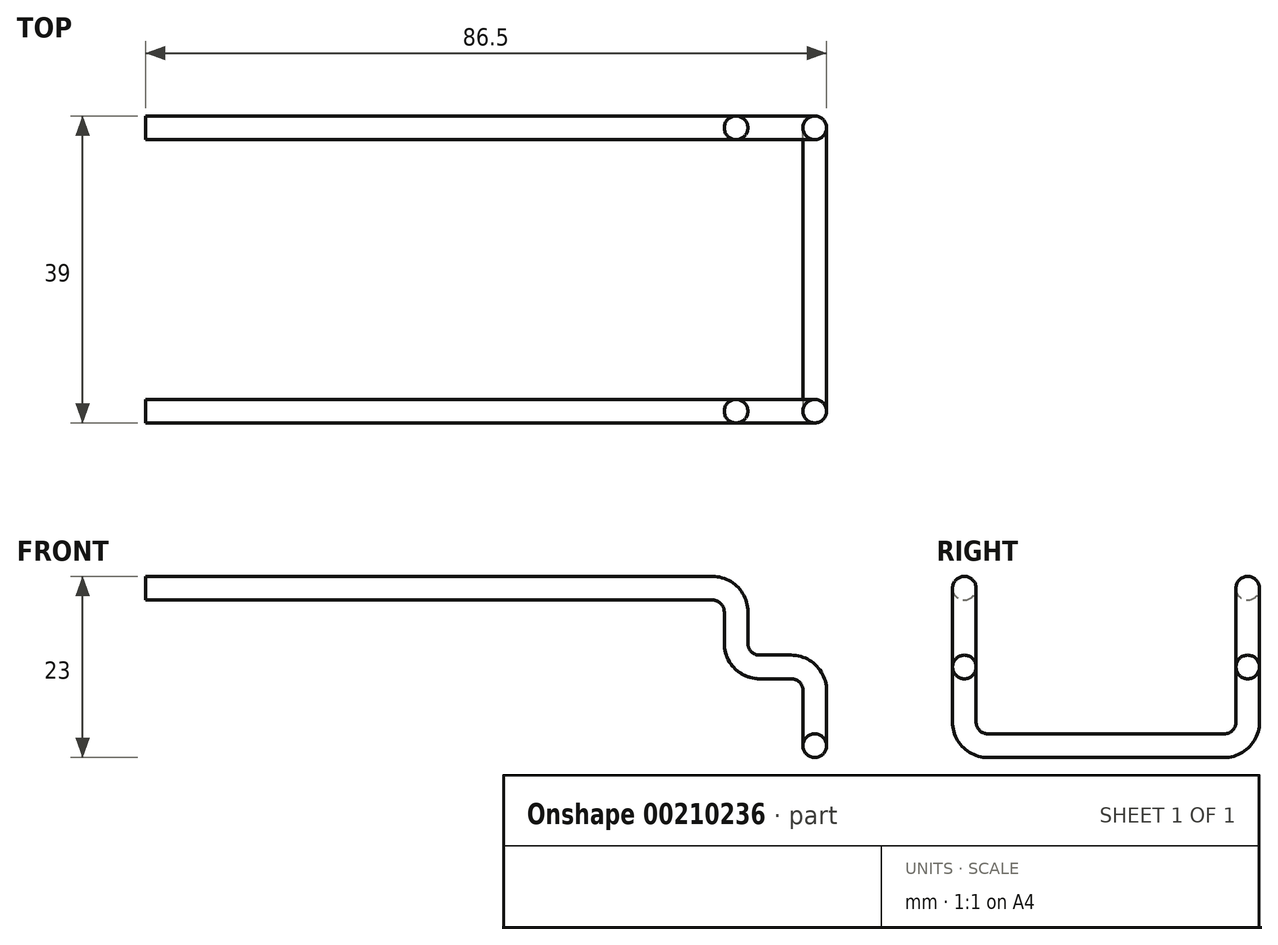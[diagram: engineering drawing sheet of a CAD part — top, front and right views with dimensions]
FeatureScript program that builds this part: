
annotation { "Feature Type Name" : "Feature", "Feature Type Description" : "" }
export const myFeature = defineFeature(function(context is Context, id is Id, definition is map)
    precondition{}
    {
        {
            var Q0;
            Q0=qCreatedBy(makeId("Front.planeOp"),FACE);
            var sketch = newSketch(context, id + "F0", { "sketchPlane" : qUnion([Q0])});
            skLineSegment(sketch, "E0", {"start": v(-46.79, 16.45) * mm, "end": v(28.21, 16.45) * mm});
            skLineSegment(sketch, "E1", {"start": v(28.21, 16.45) * mm, "end": v(28.21, 6.45) * mm});
            skLineSegment(sketch, "E2", {"start": v(28.21, 6.45) * mm, "end": v(38.21, 6.45) * mm});
            skLineSegment(sketch, "E3", {"start": v(38.21, 6.45) * mm, "end": v(38.21, -3.55) * mm});
            skLineSegment(sketch, "E4", {"start": v(38.21, -3.55) * mm, "end": v(-46.79, -3.55) * mm});
            skLineSegment(sketch, "E5", {"start": v(-46.79, -3.55) * mm, "end": v(-46.79, 16.45) * mm});
            skSolve(sketch);
        }
        {
            var Q0;
            Q0 = qSketchRegion(id + "F0", true);
            extrude(context, id + "F1", {"entities" : qUnion([Q0]), "endBound" : BoundingType.SYMMETRIC, "depth" : 36 * mm});
        }
        {
            var Q0;
            Q0=makeQuery(id+"F1.opExtrude","SWEPT_FACE",FACE,{"disambiguationData":[OSD([sQuery(id+"F0.wireOp",EDGE,"E5")])]});
            var sketch = newSketch(context, id + "F2", { "sketchPlane" : qUnion([Q0])});
            skCircle(sketch, "E6", {"center": v(18, 16.45) * mm, "radius": 1.5 * mm});
            skSolve(sketch);
        }
        {
            var Q0;
            Q0=makeQuery(id+"F1.opExtrude","SWEPT_EDGE",EDGE,{"disambiguationData":[OSD([sQuery(id+"F0.wireOp",EDGE,"E0"),sQuery(id+"F0.wireOp",EDGE,"E1")])]});
            var Q1;
            Q1=makeQuery(id+"F1.opExtrude","SWEPT_EDGE",EDGE,{"disambiguationData":[OSD([sQuery(id+"F0.wireOp",EDGE,"E1"),sQuery(id+"F0.wireOp",EDGE,"E2")])]});
            var Q2;
            Q2=makeQuery(id+"F1.opExtrude","SWEPT_EDGE",EDGE,{"disambiguationData":[OSD([sQuery(id+"F0.wireOp",EDGE,"E2"),sQuery(id+"F0.wireOp",EDGE,"E3")])]});
            var Q3;
            Q3=makeQuery(id+"F1.opExtrude","CAP_EDGE",EDGE,{"disambiguationData":[OSD([sQuery(id+"F0.wireOp",EDGE,"E4")])],"isStart":false});
            var Q4;
            Q4=makeQuery(id+"F1.opExtrude","CAP_EDGE",EDGE,{"disambiguationData":[OSD([sQuery(id+"F0.wireOp",EDGE,"E4")])],"isStart":true});
            fillet(context, id + "F3", {"entities" : qUnion([Q0, Q1, Q2, Q3, Q4]), "radius" : 3 * mm, "tangentPropagation" : true, "allowEdgeOverflow" : false});
        }
        {
            var Q0;
            Q0 = qSketchRegion(id + "F2", true);
            var Q1;
            Q1=makeQuery(id+"F1.opExtrude","CAP_EDGE",EDGE,{"disambiguationData":[OSD([sQuery(id+"F0.wireOp",EDGE,"E0")])],"isStart":false});
            var Q2;
            {var subQ0=sQuery(id+"F0.wireOp",EDGE,"E1");var subQ1=sQuery(id+"F0.wireOp",EDGE,"E0");Q2=makeQuery(id+"F3.opFillet","BLEND_EDGE",EDGE,{"blendedFrom":[makeQuery(id+"F1.opExtrude","SWEPT_EDGE",EDGE,{"disambiguationData":[OSD([subQ1,subQ0])]}),makeQuery(id+"F1.opExtrude","CAP_FACE",FACE,{"disambiguationData":[OSD([subQ1,subQ0,sQuery(id+"F0.wireOp",EDGE,"E2"),sQuery(id+"F0.wireOp",EDGE,"E3"),sQuery(id+"F0.wireOp",EDGE,"E4"),sQuery(id+"F0.wireOp",EDGE,"E5")])],"isStart":false})],"blendedInto":[makeQuery(id+"F1.opExtrude","CAP_FACE",FACE,{"disambiguationData":[OSD([subQ1,subQ0,sQuery(id+"F0.wireOp",EDGE,"E2"),sQuery(id+"F0.wireOp",EDGE,"E3"),sQuery(id+"F0.wireOp",EDGE,"E4"),sQuery(id+"F0.wireOp",EDGE,"E5")])],"isStart":false})]});}
            var Q3;
            Q3=makeQuery(id+"F1.opExtrude","CAP_EDGE",EDGE,{"disambiguationData":[OSD([sQuery(id+"F0.wireOp",EDGE,"E1")])],"isStart":false});
            var Q4;
            {var subQ0=sQuery(id+"F0.wireOp",EDGE,"E2");var subQ1=sQuery(id+"F0.wireOp",EDGE,"E1");Q4=makeQuery(id+"F3.opFillet","BLEND_EDGE",EDGE,{"blendedFrom":[makeQuery(id+"F1.opExtrude","SWEPT_EDGE",EDGE,{"disambiguationData":[OSD([subQ1,subQ0])]}),makeQuery(id+"F1.opExtrude","CAP_FACE",FACE,{"disambiguationData":[OSD([sQuery(id+"F0.wireOp",EDGE,"E0"),subQ1,subQ0,sQuery(id+"F0.wireOp",EDGE,"E3"),sQuery(id+"F0.wireOp",EDGE,"E4"),sQuery(id+"F0.wireOp",EDGE,"E5")])],"isStart":false})],"blendedInto":[makeQuery(id+"F1.opExtrude","CAP_FACE",FACE,{"disambiguationData":[OSD([sQuery(id+"F0.wireOp",EDGE,"E0"),subQ1,subQ0,sQuery(id+"F0.wireOp",EDGE,"E3"),sQuery(id+"F0.wireOp",EDGE,"E4"),sQuery(id+"F0.wireOp",EDGE,"E5")])],"isStart":false})]});}
            var Q5;
            Q5=makeQuery(id+"F1.opExtrude","CAP_EDGE",EDGE,{"disambiguationData":[OSD([sQuery(id+"F0.wireOp",EDGE,"E2")])],"isStart":false});
            var Q6;
            {var subQ0=sQuery(id+"F0.wireOp",EDGE,"E3");var subQ1=sQuery(id+"F0.wireOp",EDGE,"E2");Q6=makeQuery(id+"F3.opFillet","BLEND_EDGE",EDGE,{"blendedFrom":[makeQuery(id+"F1.opExtrude","SWEPT_EDGE",EDGE,{"disambiguationData":[OSD([subQ1,subQ0])]}),makeQuery(id+"F1.opExtrude","CAP_FACE",FACE,{"disambiguationData":[OSD([sQuery(id+"F0.wireOp",EDGE,"E0"),sQuery(id+"F0.wireOp",EDGE,"E1"),subQ1,subQ0,sQuery(id+"F0.wireOp",EDGE,"E4"),sQuery(id+"F0.wireOp",EDGE,"E5")])],"isStart":false})],"blendedInto":[makeQuery(id+"F1.opExtrude","CAP_FACE",FACE,{"disambiguationData":[OSD([sQuery(id+"F0.wireOp",EDGE,"E0"),sQuery(id+"F0.wireOp",EDGE,"E1"),subQ1,subQ0,sQuery(id+"F0.wireOp",EDGE,"E4"),sQuery(id+"F0.wireOp",EDGE,"E5")])],"isStart":false})]});}
            var Q7;
            Q7=makeQuery(id+"F1.opExtrude","CAP_EDGE",EDGE,{"disambiguationData":[OSD([sQuery(id+"F0.wireOp",EDGE,"E3")])],"isStart":false});
            var Q8;
            Q8=makeQuery(id+"F3.opFillet","BLEND_EDGE",EDGE,{"blendedFrom":[makeQuery(id+"F1.opExtrude","CAP_EDGE",EDGE,{"disambiguationData":[OSD([sQuery(id+"F0.wireOp",EDGE,"E4")])],"isStart":false}),makeQuery(id+"F1.opExtrude","SWEPT_FACE",FACE,{"disambiguationData":[OSD([sQuery(id+"F0.wireOp",EDGE,"E3")])]})],"blendedInto":[makeQuery(id+"F1.opExtrude","SWEPT_FACE",FACE,{"disambiguationData":[OSD([sQuery(id+"F0.wireOp",EDGE,"E3")])]})]});
            var Q9;
            Q9=makeQuery(id+"F1.opExtrude","SWEPT_EDGE",EDGE,{"disambiguationData":[OSD([sQuery(id+"F0.wireOp",EDGE,"E3"),sQuery(id+"F0.wireOp",EDGE,"E4")])]});
            var Q10;
            Q10=makeQuery(id+"F3.opFillet","BLEND_EDGE",EDGE,{"blendedFrom":[makeQuery(id+"F1.opExtrude","CAP_EDGE",EDGE,{"disambiguationData":[OSD([sQuery(id+"F0.wireOp",EDGE,"E4")])],"isStart":true}),makeQuery(id+"F1.opExtrude","SWEPT_FACE",FACE,{"disambiguationData":[OSD([sQuery(id+"F0.wireOp",EDGE,"E3")])]})],"blendedInto":[makeQuery(id+"F1.opExtrude","SWEPT_FACE",FACE,{"disambiguationData":[OSD([sQuery(id+"F0.wireOp",EDGE,"E3")])]})]});
            var Q11;
            Q11=makeQuery(id+"F1.opExtrude","CAP_EDGE",EDGE,{"disambiguationData":[OSD([sQuery(id+"F0.wireOp",EDGE,"E3")])],"isStart":true});
            var Q12;
            {var subQ0=sQuery(id+"F0.wireOp",EDGE,"E3");var subQ1=sQuery(id+"F0.wireOp",EDGE,"E2");Q12=makeQuery(id+"F3.opFillet","BLEND_EDGE",EDGE,{"blendedFrom":[makeQuery(id+"F1.opExtrude","SWEPT_EDGE",EDGE,{"disambiguationData":[OSD([subQ1,subQ0])]}),makeQuery(id+"F1.opExtrude","CAP_FACE",FACE,{"disambiguationData":[OSD([sQuery(id+"F0.wireOp",EDGE,"E0"),sQuery(id+"F0.wireOp",EDGE,"E1"),subQ1,subQ0,sQuery(id+"F0.wireOp",EDGE,"E4"),sQuery(id+"F0.wireOp",EDGE,"E5")])],"isStart":true})],"blendedInto":[makeQuery(id+"F1.opExtrude","CAP_FACE",FACE,{"disambiguationData":[OSD([sQuery(id+"F0.wireOp",EDGE,"E0"),sQuery(id+"F0.wireOp",EDGE,"E1"),subQ1,subQ0,sQuery(id+"F0.wireOp",EDGE,"E4"),sQuery(id+"F0.wireOp",EDGE,"E5")])],"isStart":true})]});}
            var Q13;
            Q13=makeQuery(id+"F1.opExtrude","CAP_EDGE",EDGE,{"disambiguationData":[OSD([sQuery(id+"F0.wireOp",EDGE,"E2")])],"isStart":true});
            var Q14;
            {var subQ0=sQuery(id+"F0.wireOp",EDGE,"E2");var subQ1=sQuery(id+"F0.wireOp",EDGE,"E1");Q14=makeQuery(id+"F3.opFillet","BLEND_EDGE",EDGE,{"blendedFrom":[makeQuery(id+"F1.opExtrude","SWEPT_EDGE",EDGE,{"disambiguationData":[OSD([subQ1,subQ0])]}),makeQuery(id+"F1.opExtrude","CAP_FACE",FACE,{"disambiguationData":[OSD([sQuery(id+"F0.wireOp",EDGE,"E0"),subQ1,subQ0,sQuery(id+"F0.wireOp",EDGE,"E3"),sQuery(id+"F0.wireOp",EDGE,"E4"),sQuery(id+"F0.wireOp",EDGE,"E5")])],"isStart":true})],"blendedInto":[makeQuery(id+"F1.opExtrude","CAP_FACE",FACE,{"disambiguationData":[OSD([sQuery(id+"F0.wireOp",EDGE,"E0"),subQ1,subQ0,sQuery(id+"F0.wireOp",EDGE,"E3"),sQuery(id+"F0.wireOp",EDGE,"E4"),sQuery(id+"F0.wireOp",EDGE,"E5")])],"isStart":true})]});}
            var Q15;
            Q15=makeQuery(id+"F1.opExtrude","CAP_EDGE",EDGE,{"disambiguationData":[OSD([sQuery(id+"F0.wireOp",EDGE,"E1")])],"isStart":true});
            var Q16;
            {var subQ0=sQuery(id+"F0.wireOp",EDGE,"E1");var subQ1=sQuery(id+"F0.wireOp",EDGE,"E0");Q16=makeQuery(id+"F3.opFillet","BLEND_EDGE",EDGE,{"blendedFrom":[makeQuery(id+"F1.opExtrude","SWEPT_EDGE",EDGE,{"disambiguationData":[OSD([subQ1,subQ0])]}),makeQuery(id+"F1.opExtrude","CAP_FACE",FACE,{"disambiguationData":[OSD([subQ1,subQ0,sQuery(id+"F0.wireOp",EDGE,"E2"),sQuery(id+"F0.wireOp",EDGE,"E3"),sQuery(id+"F0.wireOp",EDGE,"E4"),sQuery(id+"F0.wireOp",EDGE,"E5")])],"isStart":true})],"blendedInto":[makeQuery(id+"F1.opExtrude","CAP_FACE",FACE,{"disambiguationData":[OSD([subQ1,subQ0,sQuery(id+"F0.wireOp",EDGE,"E2"),sQuery(id+"F0.wireOp",EDGE,"E3"),sQuery(id+"F0.wireOp",EDGE,"E4"),sQuery(id+"F0.wireOp",EDGE,"E5")])],"isStart":true})]});}
            var Q17;
            Q17=makeQuery(id+"F1.opExtrude","CAP_EDGE",EDGE,{"disambiguationData":[OSD([sQuery(id+"F0.wireOp",EDGE,"E0")])],"isStart":true});
            sweep(context, id + "F4", {"profiles" : qUnion([Q0]), "path" : qUnion([Q1, Q2, Q3, Q4, Q5, Q6, Q7, Q8, Q9, Q10, Q11, Q12, Q13, Q14, Q15, Q16, Q17])});
        }
        {
            var Q0;
            Q0=makeQuery(id+"F1.opExtrude","SWEPT_BODY",BODY,{"disambiguationData":[OSD([sQuery(id+"F0.wireOp",EDGE,"E0"),sQuery(id+"F0.wireOp",EDGE,"E1"),sQuery(id+"F0.wireOp",EDGE,"E2"),sQuery(id+"F0.wireOp",EDGE,"E3"),sQuery(id+"F0.wireOp",EDGE,"E4"),sQuery(id+"F0.wireOp",EDGE,"E5")])]});
            deleteBodies(context, id + "F5", {"entities" : qUnion([Q0])});
        }
    });
